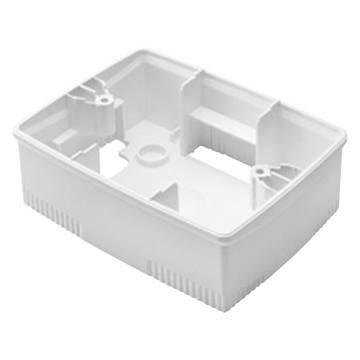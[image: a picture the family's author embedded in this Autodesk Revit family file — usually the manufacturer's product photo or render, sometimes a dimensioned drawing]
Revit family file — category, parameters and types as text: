
# Revit family: Domotics-DomesticRanges-GEWISS-CHORUS_BOX_WALLMOUNTING_WHITE
name_source: partatom
category: Apparecchi elettrici
revit_build: Autodesk Revit 2016 (Build: 20161004_0715(x64)
units: mm (PartAtom-declared; Revit-internal decimal feet)

## family parameters
Condiviso = No
Host = Superficie
Mantenere orientamento annotazione = No
Punto di calcolo locali = No
Quota connettore circolare = Usa diametro
Taglio con vuoti quando caricato = No
Tipo di parte = Normale

## types (1)
- Domotics-DomesticRanges-GEWISS-CHORUS_BOX_WALLMOUNTING_WHITE
    Altezza = 46 mm  [stored 0.150919 ft]
    Catalogue = DOMOTICS
    Catalogue Range = CHORUS - BOXES
    Characteristics = Halogen free
    Colour = White
    Description: = 4 gang
    Descrizione = WALL BOX FOR ONE PLATES, IT ST 4G WHITE
    EAN code = 8011564279339
    Electrocod = 0212
    Glow Wire Test = 650 °C
    Glow wire test: = 650 °C
    IDF = ea796d29-e1cf-482e-94f0-11c935b1ec80
    IDT = decae319-9c56-41c2-a4b3-251a3618b259
    Immagine tipo = GW16744.jpg
    Installation temperature = -5 +60 °C
    Larghezza = 90 mm
    Lunghezza = 140 mm
    Material = Technopolymer
    Modello = GW16744
    Outer dim. LxHxD (mm) = 140x90x46
    Produttore = GEWISS S.p.A.
    Prospetto di default = 1219 mm
    SEO = Box
    Standard = EN 60670-1
    Standard; = EN 60670-1
    Suitable for plates = ONE
    Support = GW16804
    Technical sheet = https://www.gewiss.com
    Thermo-pressure with ball = 70
    Torque screws tightening = 0,8NM
    URL = https://www.gewiss.com
    Version file RFA = 18.0

note: source unit labels omitted for Thermo-pressure with ball — the stored unit's dimension contradicts the parameter name (converter mislabeling)

note: [stored X ft] marks values corroborated as IEEE doubles in the binary element streams (Revit-internal decimal feet)

## geometry (parser evidence)
native form markers: Blend x4
no freeform markers — native parametric forms only
